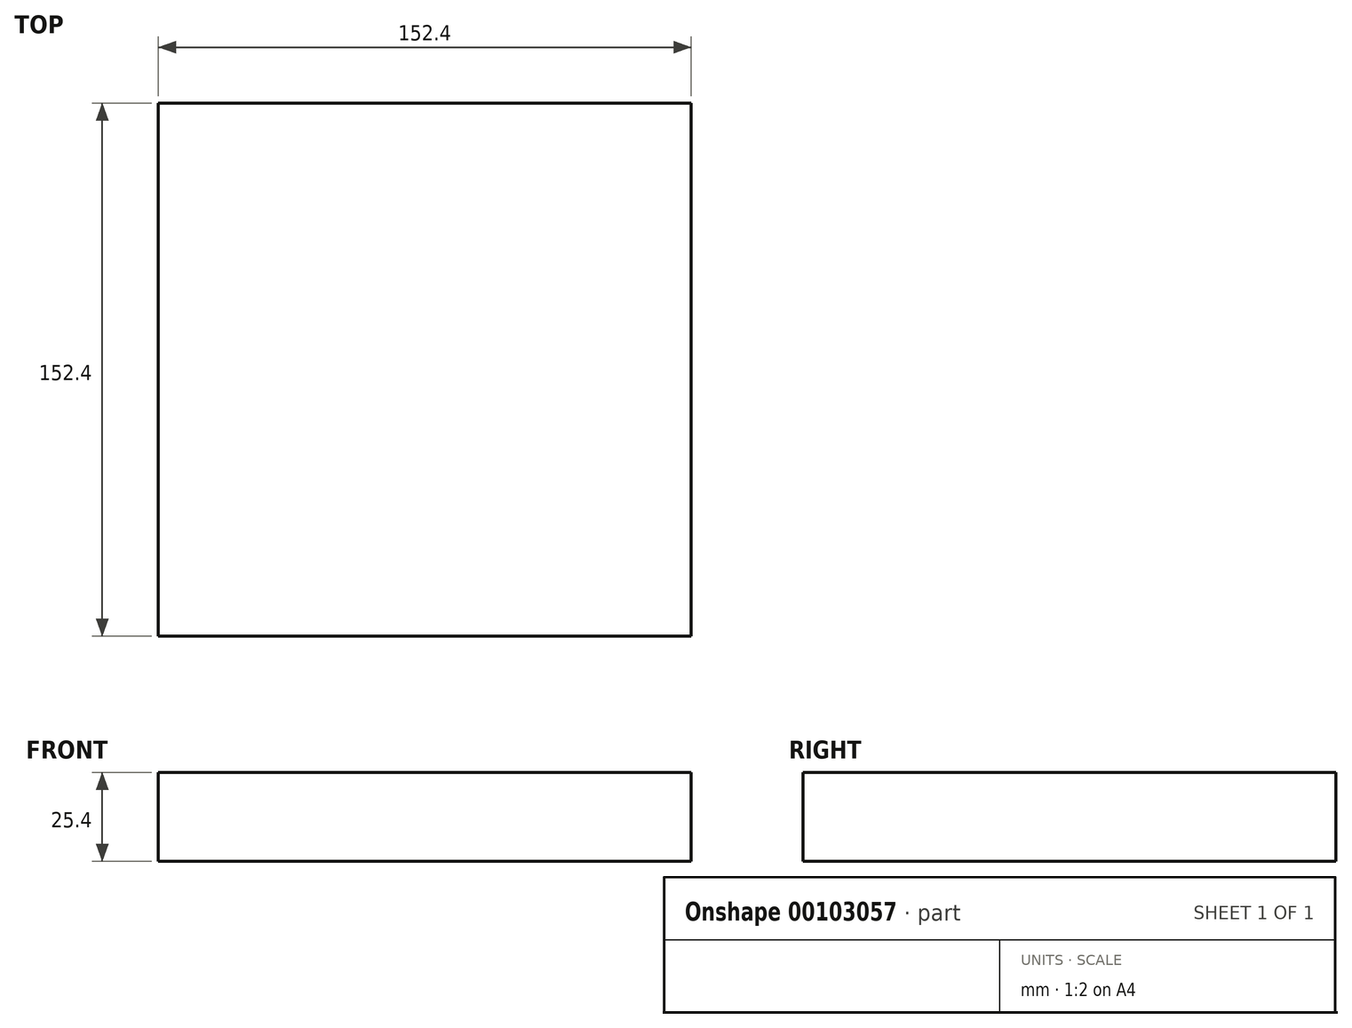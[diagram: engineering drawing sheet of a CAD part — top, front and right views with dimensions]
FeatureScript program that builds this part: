
annotation { "Feature Type Name" : "Feature", "Feature Type Description" : "" }
export const myFeature = defineFeature(function(context is Context, id is Id, definition is map)
    precondition{}
    {
        {
            var Q0;
            Q0=qCreatedBy(makeId("Top.planeOp"),FACE);
            var sketch = newSketch(context, id + "F0", { "sketchPlane" : qUnion([Q0])});
            skLineSegment(sketch, "E0.bottom", {"start": v(-35.9, 115.47) * mm, "end": v(116.5, 115.47) * mm});
            skLineSegment(sketch, "E0.top", {"start": v(-35.9, -36.93) * mm, "end": v(116.5, -36.93) * mm});
            skLineSegment(sketch, "E0.left", {"start": v(-35.9, 115.47) * mm, "end": v(-35.9, -36.93) * mm});
            skLineSegment(sketch, "E0.right", {"start": v(116.5, 115.47) * mm, "end": v(116.5, -36.93) * mm});
            skSolve(sketch);
        }
        {
            var Q0;
            Q0=makeQuery(id+"F0.imprint","IMPRINT",FACE,{"disambiguationData":[TD([[makeQuery(id+"F0.imprint","IMPRINT",EDGE,{"derivedFrom":sQuery(id+"F0.wireOp",EDGE,"E0.bottom")}),-1.0]])]});
            extrude(context, id + "F1", {"entities" : qUnion([Q0]), "depth" : 25.4 * mm});
        }
    });
